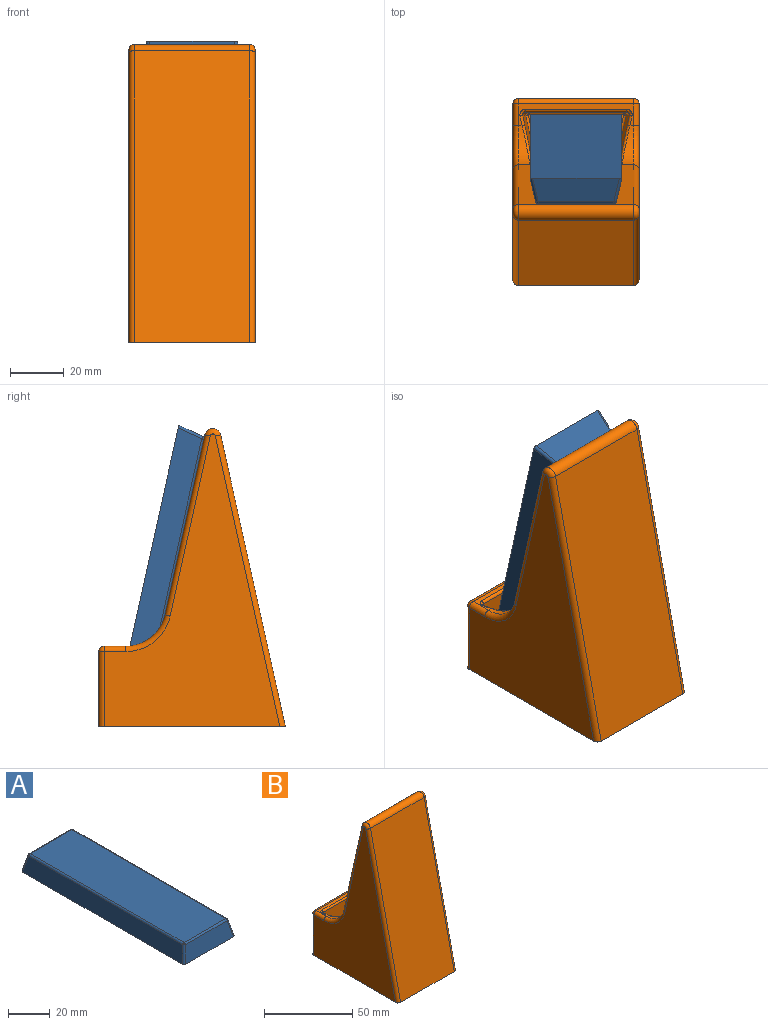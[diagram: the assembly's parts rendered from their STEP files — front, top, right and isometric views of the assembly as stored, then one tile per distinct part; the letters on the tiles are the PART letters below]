
ASSEMBLY  parts=2 mates=1
PART A: 18 faces, bbox 34.3x110x10.3 mm
  f0: plane 32.35x9.42mm, normal (0,-0.98,0.22), area 291.9mm2, adj f5,f8,f14,f17
  f1: plane 108.05x9.42mm, normal (0.98,0,0.22), area 1022mm2, adj f5,f11,f15,f17
  f2: plane 32.35x9.42mm, normal (0,0.98,0.22), area 291.9mm2, adj f5,f6,f10,f11
  f3: plane 108.05x9.42mm, normal (-0.98,0,0.22), area 1022mm2, adj f5,f6,f8,f9
  f4: plane 103.87x28.17mm, normal (0,0,1), area 2926.3mm2, adj f9,f10,f14,f15
  f5: plane 110x34.3mm, normal (0,0,-1), area 3772.2mm2, adj f0,f1,f2,f3,f6,f8,f11,f17
  f6: cylinder r=1mm len=9.58mm, axis (-0.21,0.21,-0.95), area 15.1mm2, adj f2,f3,f5,f7
  f7: sphere r=1mm, area 1.1mm2, adj f6,f9,f10
  f8: cylinder r=1mm len=9.58mm, axis (-0.21,-0.21,-0.95), area 15.1mm2, adj f0,f3,f5,f12
  f9: cylinder r=1mm len=103.87mm, axis (0,1,0), area 140.5mm2, adj f3,f4,f7,f12
  f10: cylinder r=1mm len=28.17mm, axis (-1,0,0), area 38.1mm2, adj f2,f4,f7,f13
  f11: cylinder r=1mm len=9.58mm, axis (0.21,0.21,-0.95), area 15.1mm2, adj f1,f2,f5,f13
  f12: sphere r=1mm, area 1.1mm2, adj f8,f9,f14
  f13: sphere r=1mm, area 1.1mm2, adj f10,f11,f15
  f14: cylinder r=1mm len=28.17mm, axis (-1,0,0), area 38.1mm2, adj f0,f4,f12,f16
  f15: cylinder r=1mm len=103.87mm, axis (0,1,0), area 140.5mm2, adj f1,f4,f13,f16
  f16: sphere r=1mm, area 1.1mm2, adj f14,f15,f17
  f17: cylinder r=1mm len=9.58mm, axis (0.21,-0.21,-0.95), area 15.1mm2, adj f0,f1,f5,f16
PART B: 55 faces, bbox 47.7x70.3x112.3 mm
  f0: plane 43x8.11mm, normal (0,0,1), area 98mm2, adj f15,f16,f24,f28,f32,f35,f37,f45
  f1: plane 69.8x47.19mm, normal (0,0,-1), area 1763.5mm2, adj f2,f4,f5,f6,f7,f8,f9,f10
  f2: plane 108.83x43mm, normal (0,-0.98,0.22), area 4793.1mm2, adj f1,f17,f40,f54
  f3: plane 103.71x43.67mm, normal (0,0.98,0.22), area 4118.9mm2, adj f15,f16,f17,f19,f23,f31,f36,f38
  f4: plane 109.18x65.56mm, normal (1,0,0), area 3376.2mm2, adj f1,f40,f41,f42,f43,f44,f45
  f5: plane 109.18x65.56mm, normal (-1,0,0), area 3376.2mm2, adj f1,f47,f50,f51,f52,f53,f54
  f6: plane 94.53x34.3mm, normal (0,0.98,-0.22), area 3321.2mm2, adj f1,f8,f9,f18
  f7: plane 94.53x34.3mm, normal (0,-0.98,-0.22), area 3321.2mm2, adj f1,f8,f9,f18
  f8: plane 95.32x43.87mm, normal (-1,0,0), area 2166.9mm2, adj f1,f6,f7,f18
  f9: plane 95.32x43.87mm, normal (1,0,0), area 2166.9mm2, adj f1,f6,f7,f18
  f10: plane 43x28mm, normal (0,1,0), area 1204mm2, adj f1,f44,f47,f48
  f11: plane 35.64x9.81mm, normal (0,0,1), area 328.7mm2, adj f22,f26,f30,f31
  f12: plane 37.85x23mm, normal (0,-1,0), area 845.1mm2, adj f25,f26,f32,f33
  f13: plane 29.23x16.29mm, normal (-0.98,0.21,0.05), area 312.2mm2, adj f20,f22,f23,f24,f25
  f14: plane 29.23x16.29mm, normal (0.98,0.21,0.05), area 312.2mm2, adj f30,f33,f36,f37,f39
  f15: cylinder r=15mm len=14.64mm, axis (-1,0,0), area 57mm2, adj f0,f3,f20,f43
  f16: cylinder r=15mm len=14.64mm, axis (-1,0,0), area 57mm2, adj f0,f3,f39,f51
  f17: cylinder r=3mm len=43mm, axis (-1,0,0), area 349mm2, adj f2,f3,f41,f53
  f18: cylinder r=1mm len=34.3mm, axis (1,0,0), area 92.8mm2, adj f6,f7,f8,f9
  f19: bspline ~7.2x2.44mm, area 3.1mm2, adj f3,f20,f23
  f20: bspline ~15.62x12.71mm, area 25.1mm2, adj f13,f15,f19,f24
  f21: sphere r=1mm, area 1.1mm2, adj f22,f25,f26
  f22: cylinder r=1mm len=10.02mm, axis (-0.21,-0.98,0), area 15.3mm2, adj f11,f13,f21,f27
  f23: cylinder r=1mm len=29.4mm, axis (0,0.22,-0.98), area 40.5mm2, adj f3,f13,f19,f27
  f24: cylinder r=1mm len=3.9mm, axis (0.21,0.98,0), area 5.8mm2, adj f0,f13,f20,f28
  f25: cylinder r=1mm len=23.14mm, axis (-0.05,0,-1), area 41.2mm2, adj f12,f13,f21,f28
  f26: cylinder r=1mm len=35.64mm, axis (1,0,0), area 56mm2, adj f11,f12,f21,f29
  f27: sphere r=1mm, area 1.2mm2, adj f22,f23,f31
  f28: bspline ~2.6x2.35mm, area 3.8mm2, adj f0,f24,f25,f32
  f29: sphere r=1mm, area 2.3mm2, adj f26,f30,f33
  f30: cylinder r=1mm len=10.02mm, axis (0.21,-0.98,0), area 15.3mm2, adj f11,f14,f29,f34
  f31: cylinder r=1mm len=31.4mm, axis (-1,0,0), area 42.5mm2, adj f3,f11,f27,f34
  f32: cylinder r=1mm len=37.85mm, axis (1,0,0), area 59.4mm2, adj f0,f12,f28,f35
  f33: cylinder r=1mm len=23.14mm, axis (0.05,0,-1), area 41.2mm2, adj f12,f14,f29,f35
  f34: sphere r=1mm, area 1.2mm2, adj f30,f31,f36
  f35: bspline ~2.6x2.35mm, area 3.8mm2, adj f0,f32,f33,f37
  f36: cylinder r=1mm len=29.4mm, axis (0,0.22,-0.98), area 40.5mm2, adj f3,f14,f34,f38
  f37: cylinder r=1mm len=3.9mm, axis (-0.21,0.98,0), area 5.8mm2, adj f0,f14,f35,f39
  f38: bspline ~7.2x2.44mm, area 3.1mm2, adj f3,f36,f39
  f39: bspline ~15.62x12.71mm, area 25.1mm2, adj f14,f16,f37,f38
  f40: cylinder r=2mm len=109.26mm, axis (0,0.22,0.98), area 349.5mm2, adj f1,f2,f4,f41
  f41: torus R=1mm, axis (1,0,0), area 19.3mm2, adj f4,f17,f40,f42
  f42: cylinder r=2mm len=67.51mm, axis (0,0.22,-0.98), area 215.8mm2, adj f3,f4,f41,f43
  f43: torus R=17mm, axis (1,0,0), area 66.8mm2, adj f4,f15,f42,f45
  f44: cylinder r=2mm len=28mm, axis (0,0,1), area 88mm2, adj f1,f4,f10,f46
  f45: cylinder r=2mm len=8.11mm, axis (0,-1,0), area 25.5mm2, adj f0,f4,f43,f46
  f46: sphere r=2mm, area 4mm2, adj f44,f45,f48
  f47: cylinder r=2mm len=28mm, axis (0,0,1), area 88mm2, adj f1,f5,f10,f49
  f48: cylinder r=2mm len=43mm, axis (1,0,0), area 135.1mm2, adj f0,f10,f46,f49
  f49: sphere r=2mm, area 8.6mm2, adj f47,f48,f50
  f50: cylinder r=2mm len=8.11mm, axis (0,-1,0), area 25.5mm2, adj f0,f5,f49,f51
  f51: torus R=17mm, axis (1,0,0), area 66.8mm2, adj f5,f16,f50,f52
  f52: cylinder r=2mm len=67.51mm, axis (0,-0.22,0.98), area 215.8mm2, adj f3,f5,f51,f53
  f53: torus R=1mm, axis (1,0,0), area 19.3mm2, adj f5,f17,f52,f54
  f54: cylinder r=2mm len=109.26mm, axis (0,-0.22,-0.98), area 349.5mm2, adj f1,f2,f5,f53
PLACE A rot(axis=(1,0,0),102.5deg) t=(0,24.74,58.7)mm
PLACE B t=(0,0.18,0)mm fixed
MATE fastened B.f11 <-> A.f0  axis (0,0,1) through (0,31.93,5)mm
